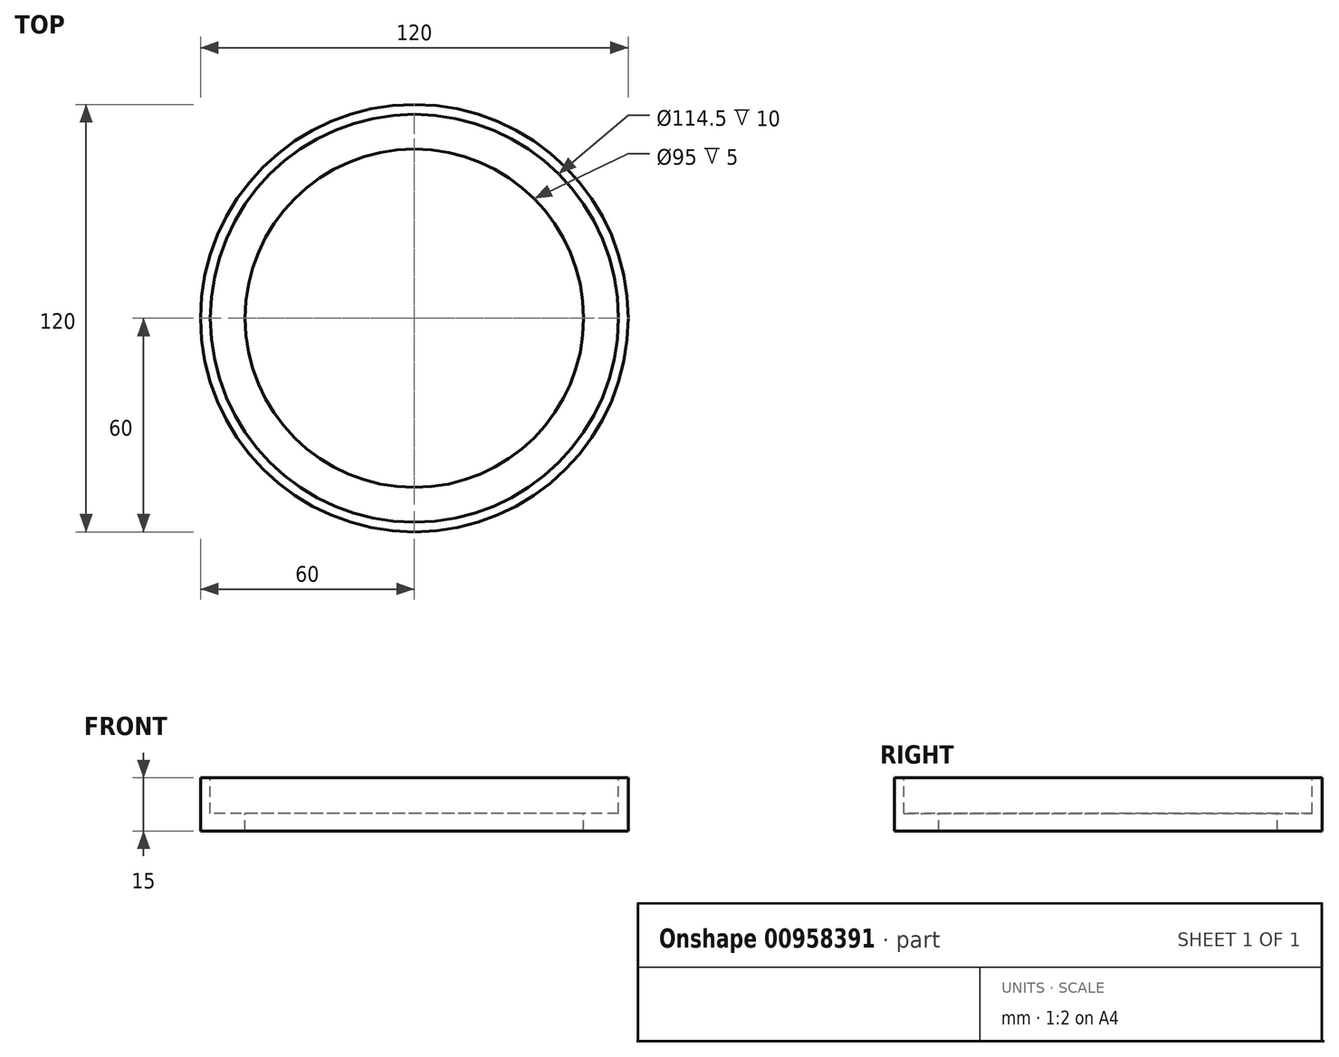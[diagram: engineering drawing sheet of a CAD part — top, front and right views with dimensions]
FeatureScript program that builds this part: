
annotation { "Feature Type Name" : "Feature", "Feature Type Description" : "" }
export const myFeature = defineFeature(function(context is Context, id is Id, definition is map)
    precondition{}
    {
        {
            var Q0;
            Q0=qCreatedBy(makeId("Front.planeOp"),FACE);
            var sketch = newSketch(context, id + "F0", { "sketchPlane" : qUnion([Q0])});
            skLineSegment(sketch, "E0", {"start": v(60, 15) * mm, "end": v(60, 0) * mm});
            skLineSegment(sketch, "E1", {"start": v(60, 15) * mm, "end": v(57.25, 15) * mm});
            skLineSegment(sketch, "E2", {"start": v(57.25, 15) * mm, "end": v(57.25, 5) * mm});
            skLineSegment(sketch, "E3", {"start": v(57.25, 5) * mm, "end": v(47.5, 5) * mm});
            skLineSegment(sketch, "E4", {"start": v(47.5, 5) * mm, "end": v(47.5, 0) * mm});
            skLineSegment(sketch, "E5", {"start": v(47.5, 0) * mm, "end": v(60, 0) * mm});
            skLineSegment(sketch, "E6", {"start": v(0, 66.4) * mm, "end": v(0, -67.67) * mm, "construction": true});
            skSolve(sketch);
        }
        {
            var Q0;
            Q0=qSketchRegion(id+"F0",true);
            var Q1;
            Q1=sQuery(id+"F0.wireOp",EDGE,"E6");
            revolve(context, id + "F1", {"surfaceOperationType" : NewSurfaceOperationType.NEW, "entities" : qUnion([Q0]), "axis" : qUnion([Q1]), "revolveType" : RevolveType.FULL});
        }
    });
